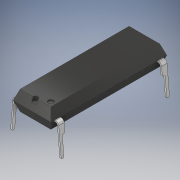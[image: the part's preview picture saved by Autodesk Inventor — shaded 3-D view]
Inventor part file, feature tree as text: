
AUTODESK INVENTOR PART (.ipt)
format: ipt  version: 2018 (Build 220112000, 112)  size: 364,544 bytes
history: native  units: in
note: dims shown in document units (in); Inventor stores cm internally (conversion verified against a paired STEP export)
features: projected_geometry x2, extrude x1, sketch x1, mirror x1
ambient origin geometry x8: Origin, YZ Plane, XZ Plane, XY Plane, X Axis, Y Axis, Z Axis, Center Point
bodies: Solid1 (feature_tree)
feature tree (5):
  extrude  "Extrusion1"  [1 undecoded]
  sketch  "Sketch1"  dims[d0=0.3937in d1=0.0in]
  projected_geometry  "Projected Loop1"
  projected_geometry  "Projected Loop2"
  mirror  "Mirror2"
note: 1 required parameter value undecoded (feature->parameter linkage not recoverable at this tier; creation-order binding heuristic only, values carry confidence <= 0.55)
